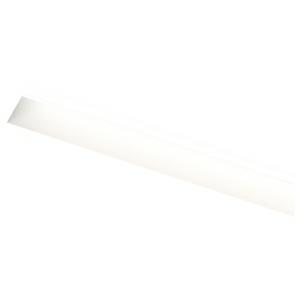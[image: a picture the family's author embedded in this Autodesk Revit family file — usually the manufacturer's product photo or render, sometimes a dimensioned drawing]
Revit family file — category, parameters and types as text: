
# Revit family: groove_l_1720_rl_led_31w_3000k_2045lm_cri80_130-0560_bdf7
name_source: partatom
category: Leuchten
revit_build: Autodesk Revit 2016 (Build: 20190508_0715(x64)
units: mm (PartAtom-declared; Revit-internal decimal feet)

## family parameters
Basisbauteil = Fläche
Beim Laden mit Abzugskörper schneiden = Nein
Bemaßung runder Anschluss = Durchmesser verwenden
Gemeinsam genutzt = Nein
Lichtquelle = Nein
Raumberechnungspunkt = Nein
Teiletyp = Normal

## types (1)
- 130-0560- (6 x LED, 710 lm, 5.1 W, 3000K)
    Beschreibung = The rimless luminaire GROOVE from the familiy GROOVE consists of aluminum-extruded profile. Charming SOFT-EDGE design ensure unparalleled styling. The ballast is integrated and allows for an operation with 220-240V (50.60Hz). GROOVE (# 130-0560) ist not dimmable (on/off). The luminaire with direct illumination and corresponds to protection class SK1 at IP20.
    CIE Flux Codes = 59 87 97 100 49
    Color Rendering = 1B/80…89
    Color Temperature = 3000K
    Height = 0 mm  [stored 0 ft]
    Hersteller = Prolicht
    Lamp Light Flux = 710 lm
    Lamp Power = 5.1 W
    Lamp count = 6
    Lampe = 6 x LED
    Length = 1720 mm
    Luminous efficacy = 67 lm/W
    ModVariant = Nein
    Modell = 130-0560
    Mounting Place = Ceiling
    Mounting Type = Recessed
    Number of Poles = 1
    OnlyDefault = Ja
    Power Factor = 1
    Product Name = GROOVE L=1720 RL LED 31W 3000K 2045lm CRI80
    Product group = Trimless recessed profile lights
    ProductGroupID = 413
    Protection Class = Protection class
    Protection Degree = Degree of protection
    RLX_Detail_Level = 1
    RlxData = <blob elided: 134921 chars, md5=134cc601>
    Scheinlast = 31 VA
    Socket = socket
    Standby Power = 0 W
    System Light Flux = 2055 lm
    System Power = 31 W
    Typenbild = 130-0560.jpg
    URL = http://relux.com
    VarID = 130-0560-
    Voltage = 0 V
    Vorgabe-Ansicht = 1800 mm
    Weight = 0.00 kg
    Width = 75 mm

note: [stored X ft] marks values corroborated as IEEE doubles in the binary element streams (Revit-internal decimal feet)

## geometry (parser evidence)
native form markers: Blend x4, Sweep x11
no freeform markers — native parametric forms only
